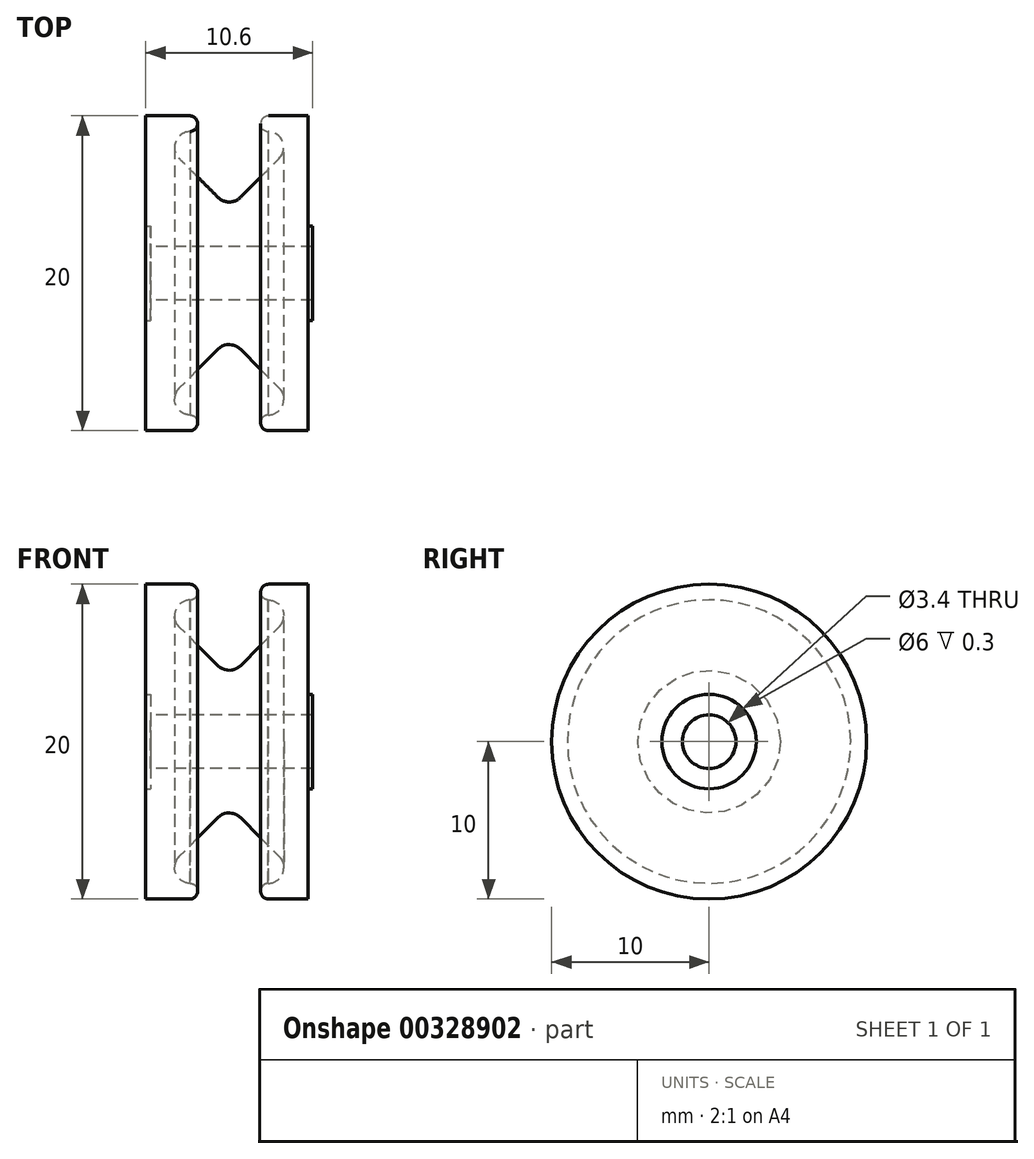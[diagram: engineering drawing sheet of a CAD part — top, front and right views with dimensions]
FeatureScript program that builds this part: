
annotation { "Feature Type Name" : "Feature", "Feature Type Description" : "" }
export const myFeature = defineFeature(function(context is Context, id is Id, definition is map)
    precondition{}
    {
        {
            var Q0;
            Q0=qCreatedBy(makeId("Front.planeOp"),FACE);
            var sketch = newSketch(context, id + "F0", { "sketchPlane" : qUnion([Q0])});
            skLineSegment(sketch, "E0", {"start": v(-5, 1.7) * mm, "end": v(-5, 10) * mm});
            skLineSegment(sketch, "E1", {"start": v(-3.18, 7.3) * mm, "end": v(-0.7, 4.82) * mm});
            skLineSegment(sketch, "E2", {"start": v(0, -6.23) * mm, "end": v(0, 31.01) * mm, "construction": true});
            skLineSegment(sketch, "E3", {"start": v(0, 0) * mm, "end": v(-27.05, 0) * mm, "construction": true});
            skPoint(sketch, "E4.visualSharp", {"position": v(0, 4.12) * mm});
            skLineSegment(sketch, "E5", {"start": v(-5, 10) * mm, "end": v(-2.5, 10) * mm});
            skPoint(sketch, "E6.newPointA", {"position": v(-5, 9) * mm});
            skPoint(sketch, "E6.newPointB", {"position": v(-5.88, 10) * mm});
            skArc(sketch, "E6.filletArc", {"start": v(-2.47, 9) * mm, "mid": v(-3.4, 8.38) * mm, "end": v(-3.18, 7.3) * mm});
            skArc(sketch, "E7", {"start": v(-2.5, 10) * mm, "mid": v(-2, 9.51) * mm, "end": v(-2.47, 9) * mm});
            skLineSegment(sketch, "E8", {"start": v(-5, 1.7) * mm, "end": v(0, 1.7) * mm});
            skLineSegment(sketch, "E9.MirrorCS", {"start": v(3.18, 7.3) * mm, "end": v(0.7, 4.82) * mm});
            skArc(sketch, "E10.MirrorCS", {"start": v(2.47, 9) * mm, "mid": v(3.4, 8.38) * mm, "end": v(3.18, 7.3) * mm});
            skArc(sketch, "E11.MirrorCS", {"start": v(2.5, 10) * mm, "mid": v(2, 9.51) * mm, "end": v(2.47, 9) * mm});
            skLineSegment(sketch, "E12.MirrorCS", {"start": v(5, 1.7) * mm, "end": v(5, 10) * mm});
            skLineSegment(sketch, "E13.MirrorCS", {"start": v(5, 1.7) * mm, "end": v(0, 1.7) * mm});
            skLineSegment(sketch, "E14.MirrorCS", {"start": v(5, 10) * mm, "end": v(2.5, 10) * mm});
            skArc(sketch, "E15.filletArc", {"start": v(-0.7, 4.82) * mm, "mid": v(0, 4.53) * mm, "end": v(0.7, 4.82) * mm});
            skSolve(sketch);
        }
        {
            var Q0;
            Q0=qCreatedBy(makeId("Right.planeOp"),FACE);
            var sketch = newSketch(context, id + "F1", { "sketchPlane" : qUnion([Q0])});
            skCircle(sketch, "E16", {"center": v(0, 0) * mm, "radius": 67.05 * mm});
            skSolve(sketch);
        }
        {
            var Q0;
            Q0=makeQuery(id+"F0.imprint","IMPRINT",FACE,{"disambiguationData":[TD([[makeQuery(id+"F0.imprint","IMPRINT",EDGE,{"derivedFrom":sQuery(id+"F0.wireOp",EDGE,"E0")}),-1.0]])]});
            var Q1;
            Q1=sQuery(id+"F1.wireOp",EDGE,"E16");
            revolve(context, id + "F2", {"entities" : qUnion([Q0]), "axis" : qUnion([Q1]), "revolveType" : RevolveType.FULL});
        }
        {
            var Q0;
            Q0=makeQuery(id+"F2.opRevolve","SWEPT_BODY",BODY,{"disambiguationData":[OSD([sQuery(id+"F0.wireOp",EDGE,"E0"),sQuery(id+"F0.wireOp",EDGE,"E1"),sQuery(id+"F0.wireOp",EDGE,"a53b7923-104e-420e-b829-f3d8ba91bc4b0.MirrorCS"),sQuery(id+"F0.wireOp",EDGE,"93a0e56a-8a41-4d58-ad07-097b1c3891bf0.MirrorCS"),sQuery(id+"F0.wireOp",EDGE,"kjfMsPoH-4s1T-tIJR-CgMq-KWpepFJFYQ97")])]});
            var Q1;
            Q1=sQuery(id+"F0.wireOp",EDGE,"E3");
            transform(context, id + "F3", {"entities" : qUnion([Q0]), "transformType" : TransformType.ROTATION, "transformAxis" : qUnion([Q1]), "angle" : 90 * degree, "makeCopy" : false});
        }
        {
            var Q0;
            Q0=makeQuery(id+"F2.opRevolve","SWEPT_FACE",FACE,{"disambiguationData":[OSD([sQuery(id+"F0.wireOp",EDGE,"E12.MirrorCS")])]});
            var sketch = newSketch(context, id + "F4", { "sketchPlane" : qUnion([Q0])});
            skCircle(sketch, "E17", {"center": v(0, 0) * mm, "radius": 3 * mm});
            skSolve(sketch);
        }
        {
            var Q0;
            Q0=makeQuery(id+"F4.imprint","IMPRINT",FACE,{"disambiguationData":[TD([[makeQuery(id+"F4.imprint","IMPRINT",EDGE,{"derivedFrom":sQuery(id+"F4.wireOp",EDGE,"E17")}),1.0]])]});
            extrude(context, id + "F5", {"entities" : qUnion([Q0]), "operationType" : NewBodyOperationType.ADD, "depth" : 0.3 * mm});
        }
        {
            var Q0;
            Q0=makeQuery(id+"F2.opRevolve","SWEPT_FACE",FACE,{"disambiguationData":[OSD([sQuery(id+"F0.wireOp",EDGE,"E0")])]});
            var sketch = newSketch(context, id + "F6", { "sketchPlane" : qUnion([Q0])});
            skCircle(sketch, "E18.0", {"center": v(0, 0) * mm, "radius": 3 * mm});
            skSolve(sketch);
        }
        {
            var Q0;
            Q0=makeQuery(id+"F6.imprint","IMPRINT",FACE,{"disambiguationData":[TD([[makeQuery(id+"F6.imprint","IMPRINT",EDGE,{"derivedFrom":sQuery(id+"F6.wireOp",EDGE,"E18.0")}),-1.0]])]});
            extrude(context, id + "F7", {"entities" : qUnion([Q0]), "operationType" : NewBodyOperationType.ADD, "depth" : 0.3 * mm});
        }
    });
